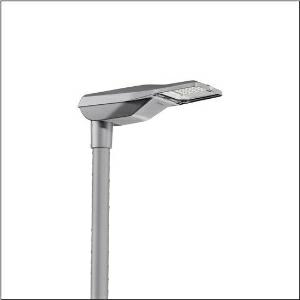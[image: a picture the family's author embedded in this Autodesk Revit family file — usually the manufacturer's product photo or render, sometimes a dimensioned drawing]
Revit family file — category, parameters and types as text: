
# Revit family: streetlight_sl_21_iq_micro___st1_5a_5xe1p31d08db_ec34
name_source: partatom
category: Lighting Fixtures
units: mm (PartAtom-declared; Revit-internal decimal feet)

## family parameters
Cut with Voids When Loaded = No
Host = Face
Light Source = No
Part Type = Normal
Room Calculation Point = No
Round Connector Dimension = Use Diameter
Shared = No

## types (1)
- --- (1 x LED, 4730 lm, 36.4 W, 3000K)
    Apparent Load = 36 VA
    CIE Flux Codes = 22 53 95 100 100
    Color Rendering = 70
    Color Temperature = 3000K
    Default Elevation = 1800 mm
    Description = Streetlight SL 21 iQ micro, mast luminaire, primary light control with lens, of PMMA, primary optical cover: cover, of toughened safety glass, transparent, light distribution: ST1.5a, light emission: direct distribution, primary light characteristic: asymmetric, installation type: post-top, side-entry, LED, High Power LED, rated luminous flux: 4.730lm, luminous efficacy: 130lm/W, light colour: 730, colour temperature: 3000K, control gear: iQ-Comfort, control: Auto-Match, Temp-Guard, Lumen-Switch, Night-Set, Smart-Wire, Light-Fading, Desk-Remote (wireless, voltage-free reading and setting of iQ features in the workshop via application-optimized NFC function/RFID function), optimised constant luminous flux control (CLO 2.0), pre-setting: linear dimming characteristic, mains connection: 220..240V, AC, 50/60Hz, start of lifetime: 36W, end of service life: 38W, reduction: 16W, luminaire housing, of diecast aluminium, powder-coated, SITECO metallic grey (DB 702S), corrosivity category C5 high according to DIN EN ISO 12944, please order mast flange separately, inclination adjustable: 0°, 5°, 10°, 15°, sealing non-destructively replaceable, multi-level sealing system, length: 528mm, width: 235mm, height: 110mm, mast flange for spigot size: 42mm (side-entry): 5XC10008XM4, 60/48mm (side-entry/post-top): 5XC10108XM2, 76/60mm (side-entry/post-top): 5XC10108XM1, protection rating (complete): IP66, insulation class (complete): insulation class II (safety insulation), certification: CE, ENEC, ENEC+, VDE, impact resistance: IK10, permissible operating ambient temperature for outdoor applications: -40..+50°C, standard-compliant lighting for roads and squares, packaging unit: 1 piece

Light Distribution: ST1.5a
    Height = 110 mm
    Lamp = 1 x LED
    Lamp Light Flux = 4730 lm
    Lamp Power = 36.4 W
    Lamp count = 1
    Length = 528 mm
    Luminous efficacy = 130 lm/W
    Manufacturer = Siteco
    ModVariant = No
    Model = 5XE1P31D08DB
    Number of Poles = 1
    OnlyDefault = Yes
    Power Factor = 1
    Product Name = Streetlight SL 21 iQ micro | ST1.5a
    Product group = mast luminaire | pylon top
    ProductGroupID = 6100
    Protection Class = Protection class II
    Protection Degree = IP 66
    RLX_Detail_Level = 1
    RLX_Emergency_Light_Flux = 0 lm
    RLX_Emergency_Type = 0
    RLX_Emergency_Type_DB = No
    RlxData = <blob elided: 103053 chars, md5=fd3e9e9b>
    Socket = socket
    Standby Power = 0 W
    System Light Flux = 4730 lm
    System Power = 36 W
    Type Comments = factory setting: luminous flux: 100 % | dim-lin: 254 | 715 mA
    Type Image = l_1006881.jpg
    URL = http://relux.com
    VarID = @adj_153393
    Voltage = 0 V
    Weight = 0.00 kg
    Width = 235 mm

## geometry (parser evidence)
native form markers: Blend x4, Sweep x8
no freeform markers — native parametric forms only
